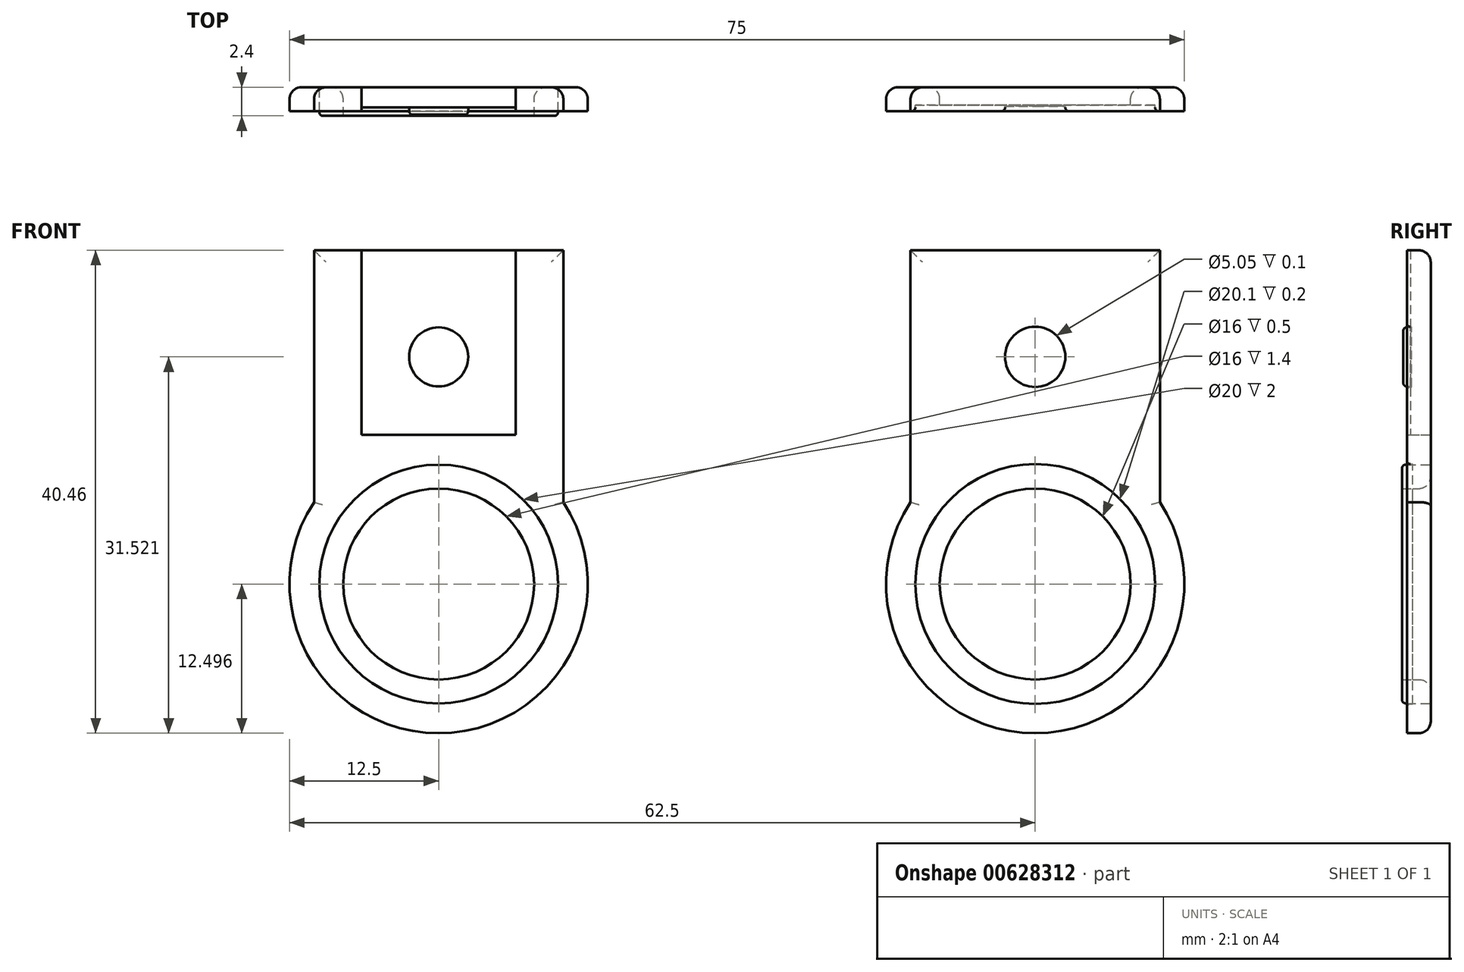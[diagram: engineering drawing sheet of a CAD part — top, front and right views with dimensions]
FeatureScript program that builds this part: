
annotation { "Feature Type Name" : "Feature", "Feature Type Description" : "" }
export const myFeature = defineFeature(function(context is Context, id is Id, definition is map)
    precondition{}
    {
        {
            var Q0;
            Q0=qCreatedBy(makeId("Front.planeOp"),FACE);
            var sketch = newSketch(context, id + "F0", { "sketchPlane" : qUnion([Q0])});
            skLineSegment(sketch, "E0.bottom", {"start": v(-6.45, 7.89) * mm, "end": v(6.45, 7.89) * mm});
            skLineSegment(sketch, "E0.left", {"start": v(-6.45, 7.89) * mm, "end": v(-6.45, -7.57) * mm});
            skLineSegment(sketch, "E0.right", {"start": v(6.45, 7.89) * mm, "end": v(6.45, -7.57) * mm});
            skCircle(sketch, "E1", {"center": v(0, -20.07) * mm, "radius": 12.5 * mm});
            skCircle(sketch, "E2", {"center": v(0, -20.07) * mm, "radius": 8 * mm});
            skLineSegment(sketch, "E3.0", {"start": v(10.45, 7.89) * mm, "end": v(10.45, -13.22) * mm});
            skLineSegment(sketch, "E3.2", {"start": v(-10.45, 7.89) * mm, "end": v(-10.45, -13.22) * mm});
            skLineSegment(sketch, "E4", {"start": v(6.45, 7.89) * mm, "end": v(10.45, 7.89) * mm});
            skLineSegment(sketch, "E5", {"start": v(-6.45, 7.89) * mm, "end": v(-10.45, 7.89) * mm});
            skLineSegment(sketch, "E6", {"start": v(-6.45, -7.57) * mm, "end": v(6.45, -7.57) * mm});
            skCircle(sketch, "E7", {"center": v(0, -1.05) * mm, "radius": 2.48 * mm});
            skLineSegment(sketch, "E8", {"start": v(0, -3.52) * mm, "end": v(0, -7.57) * mm, "construction": true});
            skLineSegment(sketch, "E9.2.0.0", {"start": v(39.55, 7.89) * mm, "end": v(39.55, -13.22) * mm});
            skLineSegment(sketch, "E9.2.0.3", {"start": v(60.45, 7.89) * mm, "end": v(60.45, -13.22) * mm});
            skCircle(sketch, "E9.2.0.7", {"center": v(50, -20.07) * mm, "radius": 12.5 * mm});
            skCircle(sketch, "E9.2.0.11", {"center": v(50, -20.07) * mm, "radius": 8 * mm});
            skLineSegment(sketch, "E10", {"start": v(39.55, 7.89) * mm, "end": v(60.45, 7.89) * mm});
            skCircle(sketch, "E11.2.0.0", {"center": v(50, -1.05) * mm, "radius": 2.52 * mm});
            skCircle(sketch, "E12.0", {"center": v(0, -20.07) * mm, "radius": 10 * mm});
            skCircle(sketch, "E13.0", {"center": v(50, -20.07) * mm, "radius": 10.05 * mm});
            skSolve(sketch);
        }
        {
            var Q0;
            {var subQ0=sQuery(id+"F0.wireOp",EDGE,"E9.2.0.0");Q0=makeQuery(id+"F0.imprint","IMPRINT",FACE,{"disambiguationData":[TD([[makeQuery(id+"F0.imprint","IMPRINT",EDGE,{"derivedFrom":subQ0}),1.0]])]});}
            var Q1;
            Q1=makeQuery(id+"F0.imprint","IMPRINT",FACE,{"disambiguationData":[TD([[makeQuery(id+"F0.imprint","IMPRINT",EDGE,{"derivedFrom":sQuery(id+"F0.wireOp",EDGE,"E13.0")}),-1.0]])]});
            var Q2;
            {var subQ4=sQuery(id+"F0.wireOp",EDGE,"E0.right");Q2=makeQuery(id+"F0.imprint","IMPRINT",FACE,{"disambiguationData":[TD([[makeQuery(id+"F0.imprint","IMPRINT",EDGE,{"derivedFrom":subQ4}),1.0]])]});}
            var Q3;
            Q3=makeQuery(id+"F0.imprint","IMPRINT",FACE,{"disambiguationData":[TD([[makeQuery(id+"F0.imprint","IMPRINT",EDGE,{"derivedFrom":sQuery(id+"F0.wireOp",EDGE,"E12.0")}),-1.0]])]});
            var Q4;
            {var subQ4=sQuery(id+"F0.wireOp",EDGE,"E0.left");Q4=makeQuery(id+"F0.imprint","IMPRINT",FACE,{"disambiguationData":[TD([[makeQuery(id+"F0.imprint","IMPRINT",EDGE,{"derivedFrom":subQ4}),-1.0]])]});}
            extrude(context, id + "F1", {"entities" : qUnion([Q0, Q1, Q2, Q3, Q4]), "depth" : 2 * mm, "offsetDistance" : 25 * mm});
        }
        {
            var Q0;
            Q0=makeQuery(id+"F0.imprint","IMPRINT",FACE,{"disambiguationData":[TD([[makeQuery(id+"F0.imprint","IMPRINT",EDGE,{"derivedFrom":sQuery(id+"F0.wireOp",EDGE,"E0.bottom")}),-1.0]])]});
            extrude(context, id + "F2", {"entities" : qUnion([Q0]), "depth" : 1.7 * mm, "offsetDistance" : 25 * mm});
        }
        {
            var Q0;
            Q0=makeQuery(id+"F0.imprint","IMPRINT",FACE,{"disambiguationData":[TD([[makeQuery(id+"F0.imprint","IMPRINT",EDGE,{"derivedFrom":sQuery(id+"F0.wireOp",EDGE,"E7")}),1.0]])]});
            extrude(context, id + "F3", {"entities" : qUnion([Q0]), "operationType" : NewBodyOperationType.ADD, "depth" : 2.3 * mm, "offsetDistance" : 25 * mm});
        }
        {
            var Q0;
            Q0=makeQuery(id+"F0.imprint","IMPRINT",FACE,{"disambiguationData":[TD([[makeQuery(id+"F0.imprint","IMPRINT",EDGE,{"derivedFrom":sQuery(id+"F0.wireOp",EDGE,"E11.2.0.0")}),1.0]])]});
            extrude(context, id + "F4", {"entities" : qUnion([Q0]), "operationType" : NewBodyOperationType.ADD, "depth" : 1.6 * mm, "offsetDistance" : 25 * mm});
        }
        {
            var Q0;
            Q0=makeQuery(id+"F1.opExtrude","CAP_EDGE",EDGE,{"disambiguationData":[OSD([sQuery(id+"F0.wireOp",EDGE,"E11.2.0.0")])],"isStart":false});
            var Q1;
            Q1=makeQuery(id+"F3.opExtrude","CAP_EDGE",EDGE,{"disambiguationData":[OSD([sQuery(id+"F0.wireOp",EDGE,"E7")])],"isStart":false});
            fillet(context, id + "F5", {"entities" : qUnion([Q0, Q1]), "radius" : 0.3 * mm, "tangentPropagation" : true, "allowEdgeOverflow" : false});
        }
        {
            var Q0;
            Q0=makeQuery(id+"F0.imprint","IMPRINT",FACE,{"disambiguationData":[TD([[makeQuery(id+"F0.imprint","IMPRINT",EDGE,{"derivedFrom":sQuery(id+"F0.wireOp",EDGE,"E2")}),-1.0]])]});
            extrude(context, id + "F6", {"entities" : qUnion([Q0]), "depth" : 2.4 * mm, "offsetDistance" : 25 * mm});
        }
        {
            var Q0;
            Q0=makeQuery(id+"F0.imprint","IMPRINT",FACE,{"disambiguationData":[TD([[makeQuery(id+"F0.imprint","IMPRINT",EDGE,{"derivedFrom":sQuery(id+"F0.wireOp",EDGE,"E9.2.0.11")}),-1.0]])]});
            extrude(context, id + "F7", {"entities" : qUnion([Q0]), "operationType" : NewBodyOperationType.ADD, "depth" : 1.5 * mm, "offsetDistance" : 25 * mm});
        }
        {
            var Q0;
            Q0=makeQuery(id+"F1.opExtrude","CAP_EDGE",EDGE,{"disambiguationData":[OSD([sQuery(id+"F0.wireOp",EDGE,"E9.2.0.0")])],"isStart":true});
            var Q1;
            Q1=makeQuery(id+"F1.opExtrude","CAP_EDGE",EDGE,{"disambiguationData":[OSD([sQuery(id+"F0.wireOp",EDGE,"E1")])],"isStart":true});
            var Q2;
            Q2=makeQuery(id+"F1.opExtrude","CAP_EDGE",EDGE,{"disambiguationData":[OSD([sQuery(id+"F0.wireOp",EDGE,"E3.0")])],"isStart":true});
            var Q3;
            Q3=makeQuery(id+"F1.opExtrude","CAP_EDGE",EDGE,{"disambiguationData":[OSD([sQuery(id+"F0.wireOp",EDGE,"E4")])],"isStart":true});
            var Q4;
            Q4=makeQuery(id+"F1.opExtrude","CAP_EDGE",EDGE,{"disambiguationData":[OSD([sQuery(id+"F0.wireOp",EDGE,"E5")])],"isStart":true});
            var Q5;
            Q5=makeQuery(id+"F1.opExtrude","CAP_EDGE",EDGE,{"disambiguationData":[OSD([sQuery(id+"F0.wireOp",EDGE,"E3.2")])],"isStart":true});
            var Q6;
            Q6=makeQuery(id+"F2.opExtrude","CAP_EDGE",EDGE,{"disambiguationData":[OSD([sQuery(id+"F0.wireOp",EDGE,"E0.bottom")])],"isStart":true});
            var Q7;
            Q7=makeQuery(id+"F1.opExtrude","CAP_EDGE",EDGE,{"disambiguationData":[OSD([sQuery(id+"F0.wireOp",EDGE,"E2")])],"isStart":true});
            var Q8;
            Q8=makeQuery(id+"F1.opExtrude","CAP_EDGE",EDGE,{"disambiguationData":[OSD([sQuery(id+"F0.wireOp",EDGE,"E9.2.0.7")])],"isStart":true});
            var Q9;
            Q9=makeQuery(id+"F1.opExtrude","CAP_EDGE",EDGE,{"disambiguationData":[OSD([sQuery(id+"F0.wireOp",EDGE,"E9.2.0.3")])],"isStart":true});
            var Q10;
            Q10=makeQuery(id+"F1.opExtrude","CAP_EDGE",EDGE,{"disambiguationData":[OSD([sQuery(id+"F0.wireOp",EDGE,"E10")])],"isStart":true});
            var Q11;
            Q11=makeQuery(id+"F7.opExtrude","CAP_EDGE",EDGE,{"disambiguationData":[OSD([sQuery(id+"F0.wireOp",EDGE,"E9.2.0.11")])],"isStart":true});
            var Q12;
            Q12=makeQuery(id+"F6.opExtrude","CAP_EDGE",EDGE,{"disambiguationData":[OSD([sQuery(id+"F0.wireOp",EDGE,"E2")])],"isStart":true});
            fillet(context, id + "F8", {"entities" : qUnion([Q0, Q1, Q2, Q3, Q4, Q5, Q6, Q7, Q8, Q9, Q10, Q11, Q12]), "radius" : 1 * mm, "tangentPropagation" : true, "allowEdgeOverflow" : false});
        }
        {
            var Q0;
            Q0=makeQuery(id+"F1.opExtrude","CAP_EDGE",EDGE,{"disambiguationData":[OSD([sQuery(id+"F0.wireOp",EDGE,"E13.0")])],"isStart":false});
            fillet(context, id + "F9", {"entities" : qUnion([Q0]), "radius" : 0.3 * mm, "tangentPropagation" : true, "allowEdgeOverflow" : false});
        }
        {
            var Q0;
            Q0=makeQuery(id+"F6.opExtrude","CAP_EDGE",EDGE,{"disambiguationData":[OSD([sQuery(id+"F0.wireOp",EDGE,"E12.0")])],"isStart":false});
            fillet(context, id + "F10", {"entities" : qUnion([Q0]), "radius" : 0.3 * mm, "tangentPropagation" : true, "allowEdgeOverflow" : false});
        }
    });
